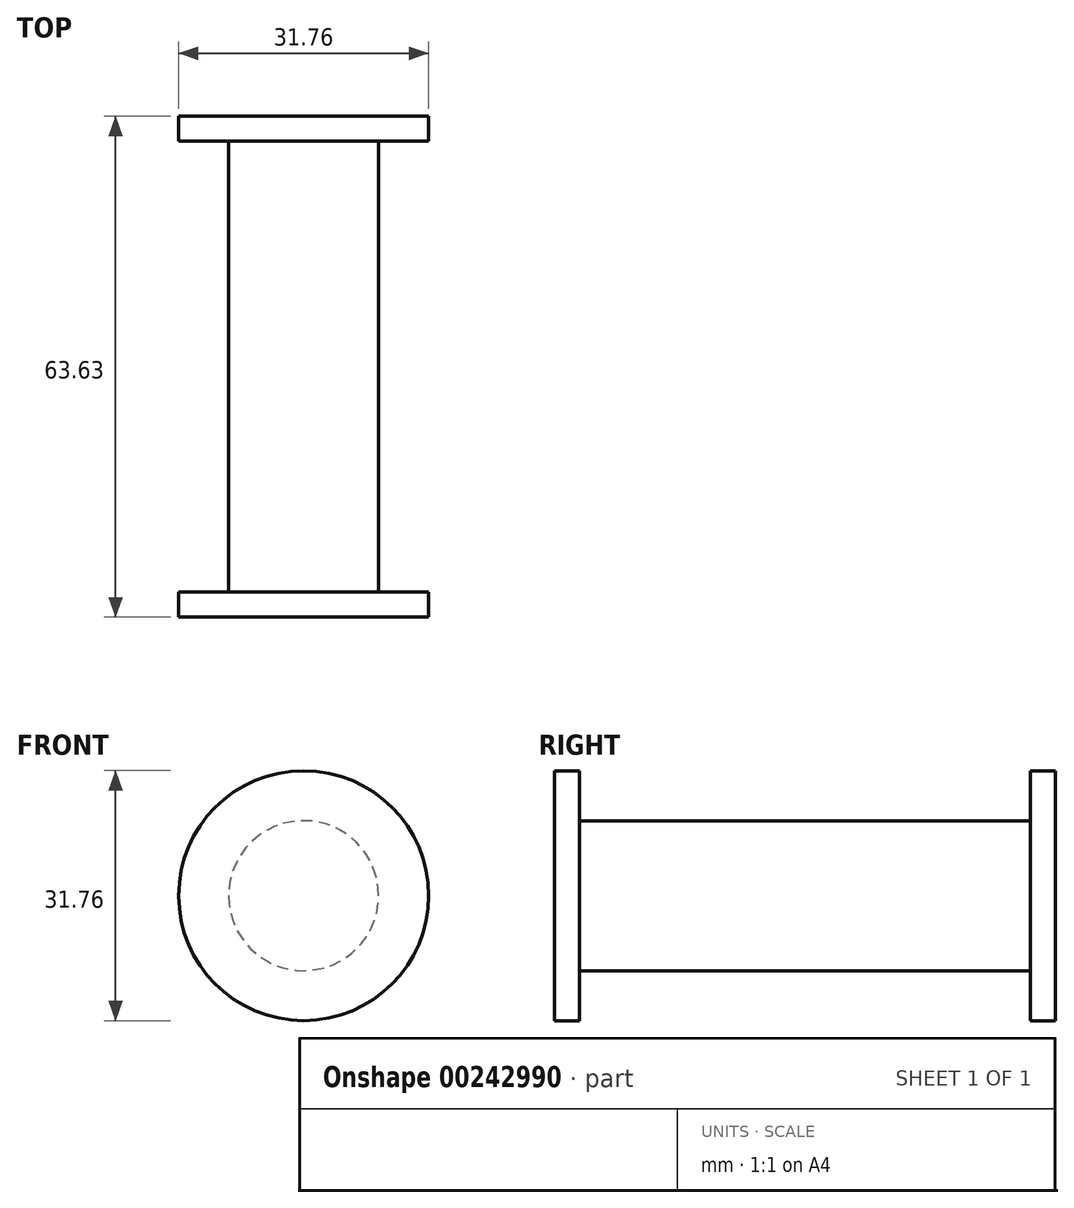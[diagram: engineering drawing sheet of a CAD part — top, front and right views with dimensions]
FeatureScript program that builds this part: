
annotation { "Feature Type Name" : "Feature", "Feature Type Description" : "" }
export const myFeature = defineFeature(function(context is Context, id is Id, definition is map)
    precondition{}
    {
        {
            var Q0;
            Q0=qCreatedBy(makeId("Right.planeOp"),FACE);
            var sketch = newSketch(context, id + "F0", { "sketchPlane" : qUnion([Q0])});
            skLineSegment(sketch, "E0", {"start": v(0, 0) * mm, "end": v(-48.33, 0) * mm, "construction": true});
            skLineSegment(sketch, "E1", {"start": v(0, 0) * mm, "end": v(0, 15.88) * mm});
            skLineSegment(sketch, "E2", {"start": v(0, 15.88) * mm, "end": v(-3.18, 15.88) * mm});
            skLineSegment(sketch, "E3", {"start": v(-3.18, 15.88) * mm, "end": v(-3.18, 9.53) * mm});
            skLineSegment(sketch, "E4", {"start": v(-3.18, 9.53) * mm, "end": v(-60.45, 9.52) * mm});
            skLineSegment(sketch, "E5", {"start": v(-60.45, 9.52) * mm, "end": v(-60.45, 15.87) * mm});
            skLineSegment(sketch, "E6", {"start": v(-60.45, 15.87) * mm, "end": v(-63.63, 15.87) * mm});
            skLineSegment(sketch, "E7", {"start": v(-63.63, 15.87) * mm, "end": v(-63.63, 0) * mm});
            skLineSegment(sketch, "E8", {"start": v(-63.63, 0) * mm, "end": v(0, 0) * mm});
            skSolve(sketch);
        }
        {
            var Q0;
            Q0 = qSketchRegion(id + "F0", true);
            var Q1;
            Q1=sQuery(id+"F0.wireOp",EDGE,"E8");
            revolve(context, id + "F1", {"entities" : qUnion([Q0]), "axis" : qUnion([Q1]), "revolveType" : RevolveType.FULL});
        }
    });
